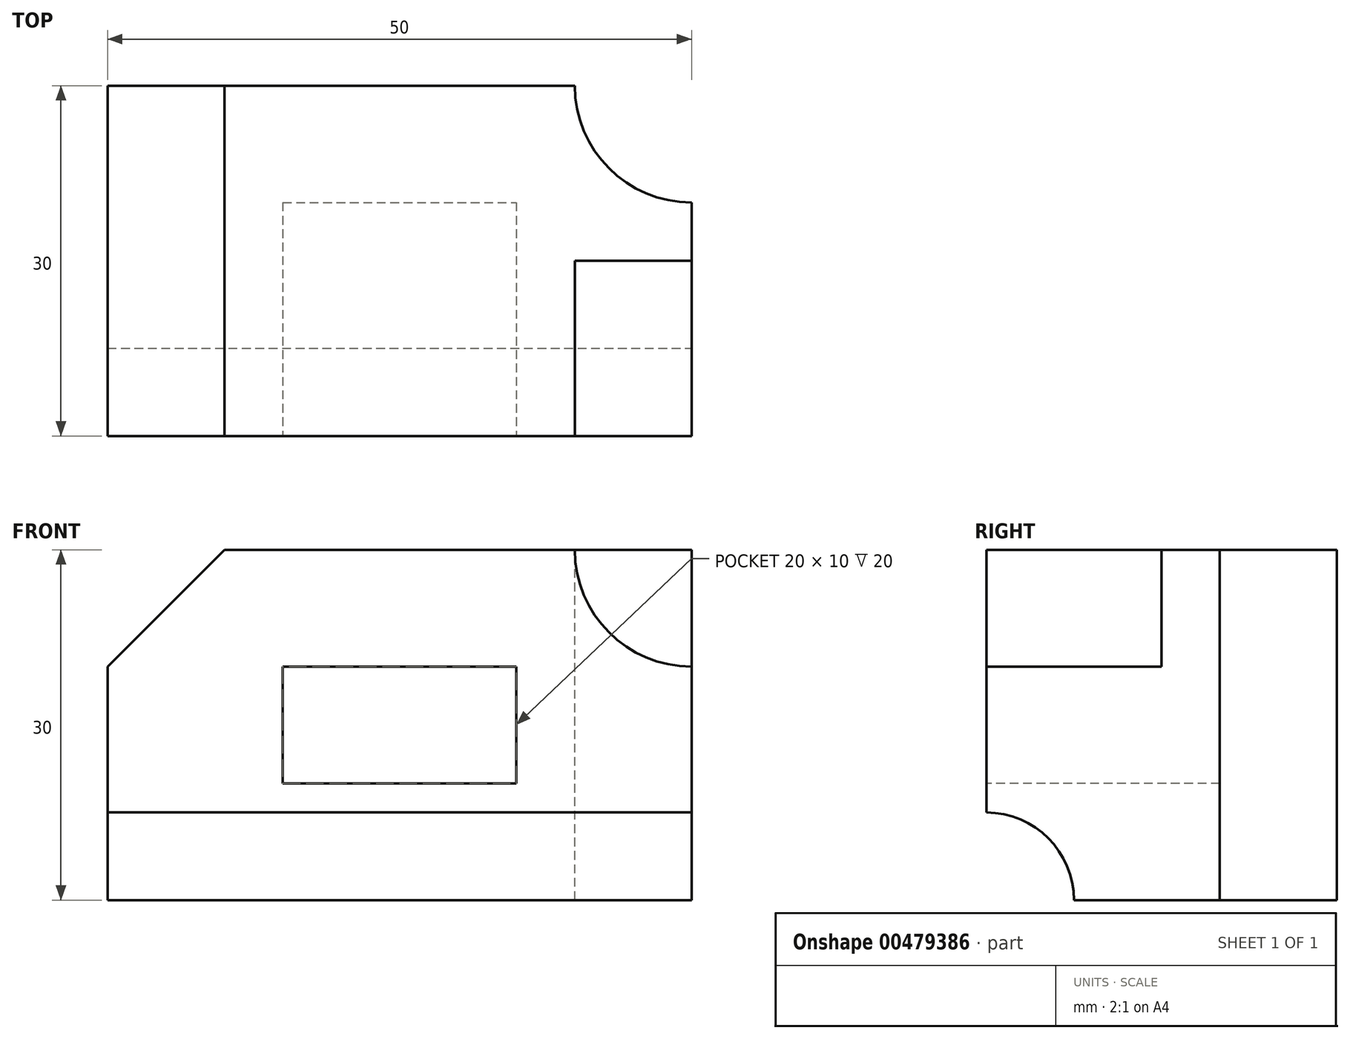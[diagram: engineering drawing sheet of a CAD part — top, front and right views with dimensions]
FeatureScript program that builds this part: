
annotation { "Feature Type Name" : "Feature", "Feature Type Description" : "" }
export const myFeature = defineFeature(function(context is Context, id is Id, definition is map)
    precondition{}
    {
        {
            var Q0;
            Q0=qCreatedBy(makeId("Top.planeOp"),FACE);
            var sketch = newSketch(context, id + "F0", { "sketchPlane" : qUnion([Q0])});
            skLineSegment(sketch, "E0.bottom", {"start": v(0, 0) * mm, "end": v(50, 0) * mm});
            skLineSegment(sketch, "E0.top", {"start": v(0, 30) * mm, "end": v(50, 30) * mm});
            skLineSegment(sketch, "E0.left", {"start": v(0, 0) * mm, "end": v(0, 30) * mm});
            skLineSegment(sketch, "E0.right", {"start": v(50, 0) * mm, "end": v(50, 30) * mm});
            skSolve(sketch);
        }
        {
            var Q0;
            Q0 = qSketchRegion(id + "F0", true);
            extrude(context, id + "F1", {"entities" : qUnion([Q0]), "depth" : 30 * mm});
        }
        {
            var Q0;
            Q0=makeQuery(id+"F1.opExtrude","SWEPT_FACE",FACE,{"disambiguationData":[OSD([sQuery(id+"F0.wireOp",EDGE,"E0.bottom")])]});
            var sketch = newSketch(context, id + "F2", { "sketchPlane" : qUnion([Q0])});
            skLineSegment(sketch, "E1", {"start": v(0, 30) * mm, "end": v(0, 20) * mm});
            skLineSegment(sketch, "E2", {"start": v(0, 30) * mm, "end": v(10, 30) * mm});
            skLineSegment(sketch, "E3", {"start": v(10, 30) * mm, "end": v(0, 20) * mm});
            skSolve(sketch);
        }
        {
            var Q0;
            Q0 = qSketchRegion(id + "F2", true);
            extrude(context, id + "F3", {"entities" : qUnion([Q0]), "operationType" : NewBodyOperationType.REMOVE, "endBound" : BoundingType.THROUGH_ALL, "oppositeDirection" : true, "depth" : 25 * mm});
        }
        {
            var Q0;
            Q0=makeQuery(id+"F1.opExtrude","SWEPT_FACE",FACE,{"disambiguationData":[OSD([sQuery(id+"F0.wireOp",EDGE,"E0.bottom")])]});
            var sketch = newSketch(context, id + "F4", { "sketchPlane" : qUnion([Q0])});
            skCircle(sketch, "E4", {"center": v(50, 30) * mm, "radius": 10 * mm});
            skSolve(sketch);
        }
        {
            var Q0;
            Q0 = qSketchRegion(id + "F4", true);
            extrude(context, id + "F5", {"entities" : qUnion([Q0]), "operationType" : NewBodyOperationType.REMOVE, "oppositeDirection" : true, "depth" : 15 * mm});
        }
        {
            var Q0;
            Q0=makeQuery(id+"F1.opExtrude","SWEPT_FACE",FACE,{"disambiguationData":[OSD([sQuery(id+"F0.wireOp",EDGE,"E0.bottom")])]});
            var sketch = newSketch(context, id + "F6", { "sketchPlane" : qUnion([Q0])});
            skLineSegment(sketch, "E5.bottom", {"start": v(15, 10) * mm, "end": v(35, 10) * mm});
            skLineSegment(sketch, "E5.top", {"start": v(15, 20) * mm, "end": v(35, 20) * mm});
            skLineSegment(sketch, "E5.left", {"start": v(15, 10) * mm, "end": v(15, 20) * mm});
            skLineSegment(sketch, "E5.right", {"start": v(35, 10) * mm, "end": v(35, 20) * mm});
            skSolve(sketch);
        }
        {
            var Q0;
            Q0 = qSketchRegion(id + "F6", true);
            extrude(context, id + "F7", {"entities" : qUnion([Q0]), "operationType" : NewBodyOperationType.REMOVE, "oppositeDirection" : true, "depth" : 20 * mm});
        }
        {
            var Q0;
            Q0=makeQuery(id+"F1.opExtrude","SWEPT_FACE",FACE,{"disambiguationData":[OSD([sQuery(id+"F0.wireOp",EDGE,"E0.right")])]});
            var sketch = newSketch(context, id + "F8", { "sketchPlane" : qUnion([Q0])});
            skCircle(sketch, "E6", {"center": v(0, 0) * mm, "radius": 7.5 * mm});
            skSolve(sketch);
        }
        {
            var Q0;
            Q0 = qSketchRegion(id + "F8", true);
            extrude(context, id + "F9", {"entities" : qUnion([Q0]), "operationType" : NewBodyOperationType.REMOVE, "endBound" : BoundingType.THROUGH_ALL, "oppositeDirection" : true, "depth" : 25 * mm});
        }
        {
            var Q0;
            Q0=makeQuery(id+"F1.opExtrude","CAP_FACE",FACE,{"disambiguationData":[OSD([sQuery(id+"F0.wireOp",EDGE,"E0.bottom"),sQuery(id+"F0.wireOp",EDGE,"E0.top"),sQuery(id+"F0.wireOp",EDGE,"E0.left"),sQuery(id+"F0.wireOp",EDGE,"E0.right")])],"isStart":false});
            var sketch = newSketch(context, id + "F10", { "sketchPlane" : qUnion([Q0])});
            skCircle(sketch, "E7", {"center": v(50, 30) * mm, "radius": 10 * mm});
            skSolve(sketch);
        }
        {
            var Q0;
            Q0 = qSketchRegion(id + "F10", true);
            extrude(context, id + "F11", {"entities" : qUnion([Q0]), "operationType" : NewBodyOperationType.REMOVE, "endBound" : BoundingType.THROUGH_ALL, "oppositeDirection" : true, "depth" : 25 * mm});
        }
    });
